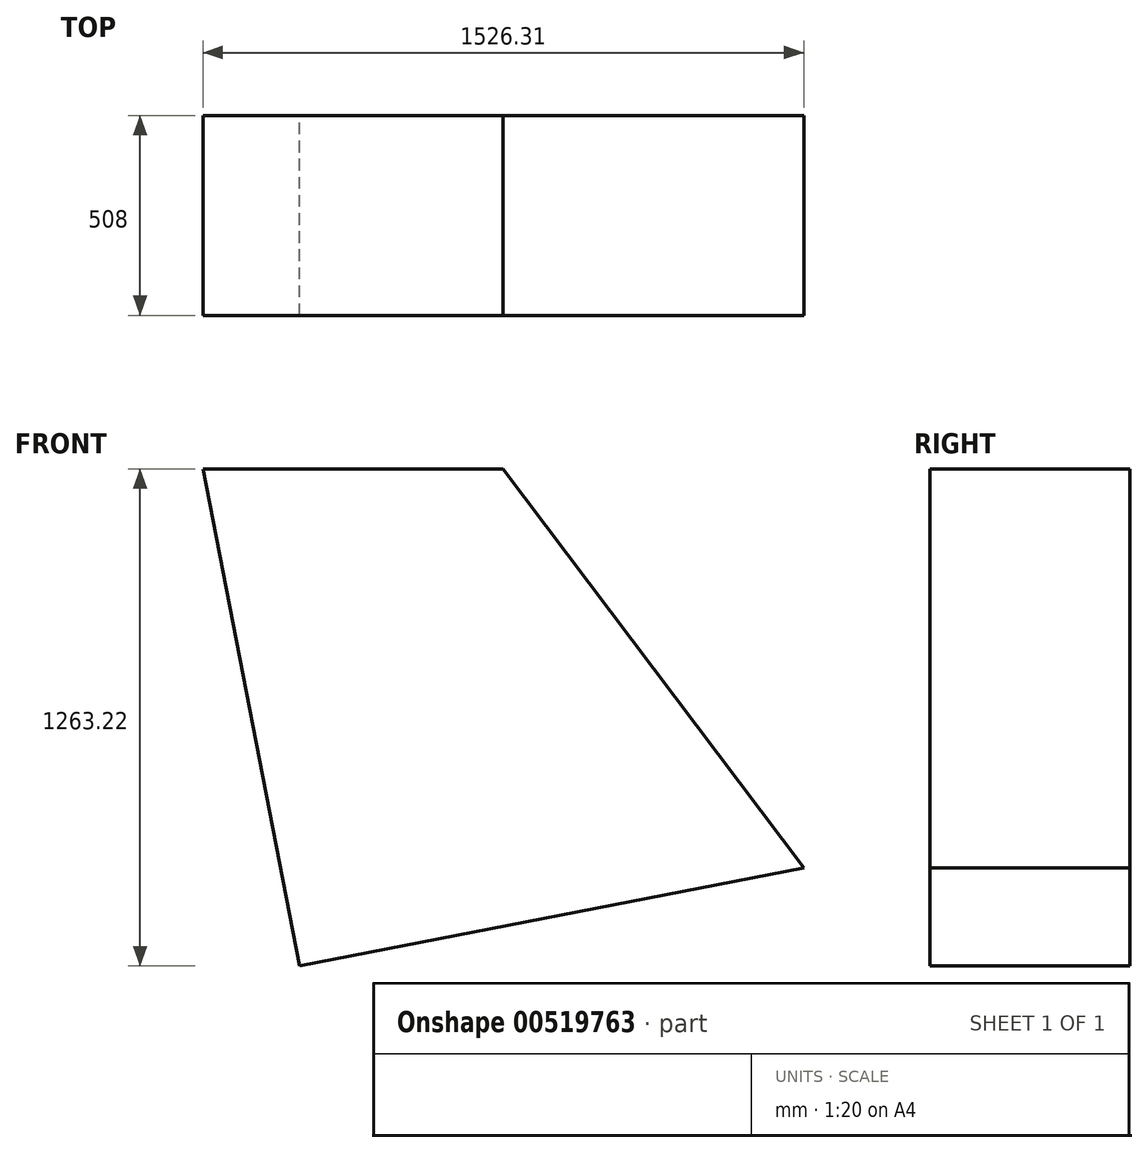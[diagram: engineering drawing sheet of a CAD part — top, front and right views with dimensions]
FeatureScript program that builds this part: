
annotation { "Feature Type Name" : "Feature", "Feature Type Description" : "" }
export const myFeature = defineFeature(function(context is Context, id is Id, definition is map)
    precondition{}
    {
        {
            var Q0;
            Q0=qCreatedBy(makeId("Front.planeOp"),FACE);
            var sketch = newSketch(context, id + "F0", { "sketchPlane" : qUnion([Q0])});
            skLineSegment(sketch, "E0", {"start": v(0, 62.52) * mm, "end": v(762, 62.52) * mm});
            skLineSegment(sketch, "E1", {"start": v(762, 62.52) * mm, "end": v(1526.3, -951.75) * mm});
            skLineSegment(sketch, "E2", {"start": v(0, 62.52) * mm, "end": v(245.55, -1200.7) * mm});
            skLineSegment(sketch, "E3", {"start": v(245.55, -1200.7) * mm, "end": v(1526.3, -951.75) * mm});
            skSolve(sketch);
        }
        {
            var Q0;
            Q0 = qSketchRegion(id + "F0", true);
            extrude(context, id + "F1", {"entities" : qUnion([Q0]), "depth" : 508 * mm, "offsetDistance" : 25.4 * mm});
        }
    });
